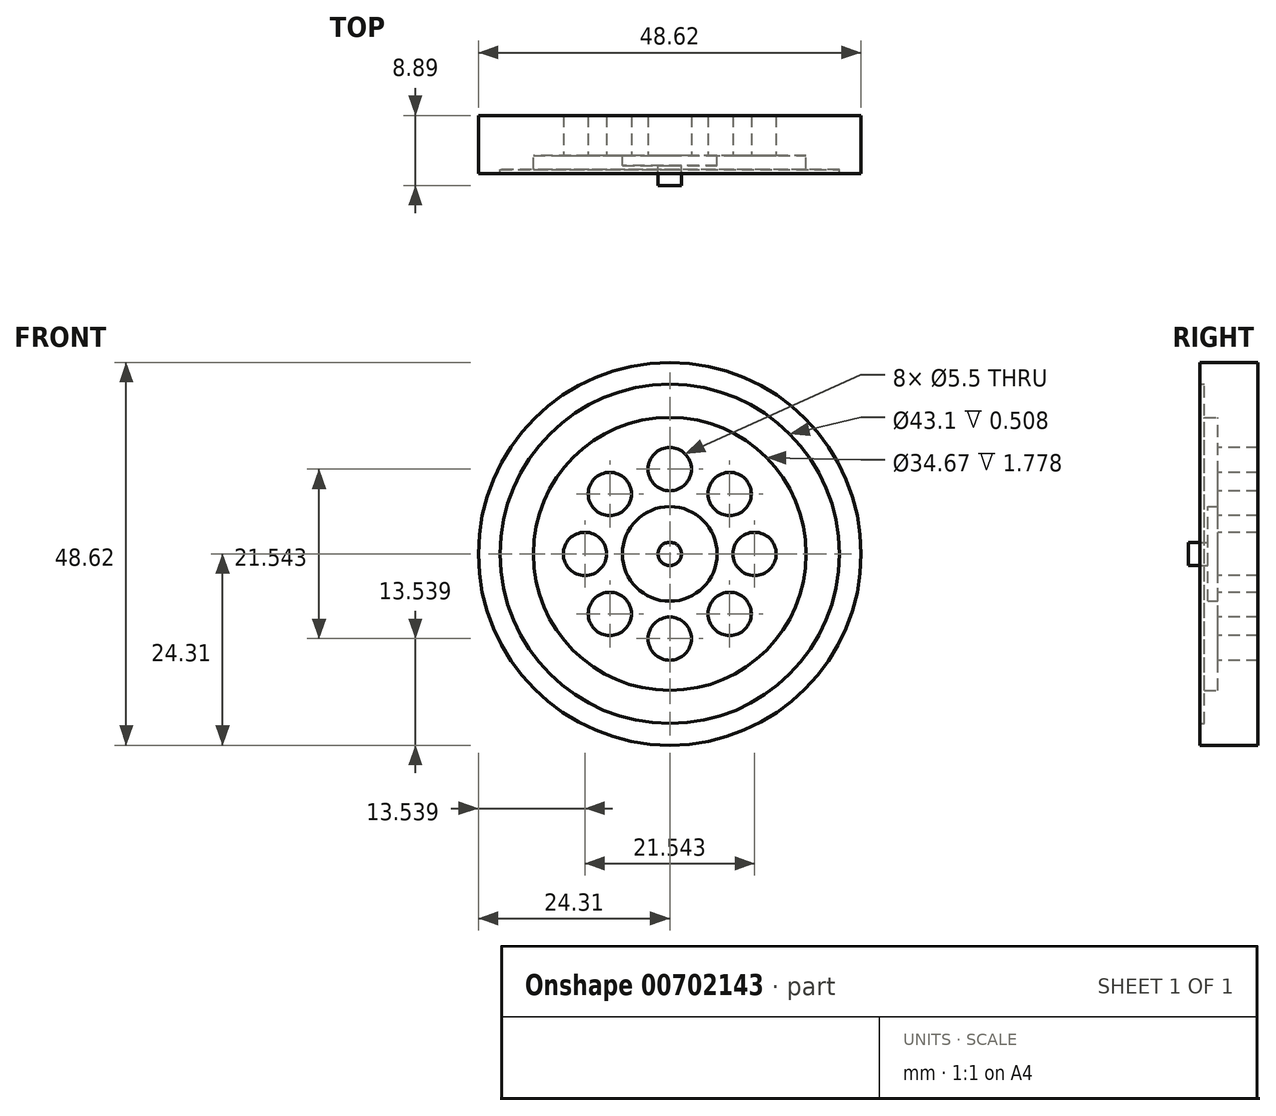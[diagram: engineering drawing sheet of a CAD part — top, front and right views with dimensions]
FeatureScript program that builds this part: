
annotation { "Feature Type Name" : "Feature", "Feature Type Description" : "" }
export const myFeature = defineFeature(function(context is Context, id is Id, definition is map)
    precondition{}
    {
        {
            var Q0;
            Q0=qCreatedBy(makeId("Front.planeOp"),FACE);
            var sketch = newSketch(context, id + "F0", { "sketchPlane" : qUnion([Q0])});
            skCircle(sketch, "E0", {"center": v(0, 0) * mm, "radius": 24.3 * mm});
            skSolve(sketch);
        }
        {
            var Q0;
            Q0=makeQuery(id+"F0.imprint","IMPRINT",FACE,{"disambiguationData":[TD([[makeQuery(id+"F0.imprint","IMPRINT",EDGE,{"derivedFrom":sQuery(id+"F0.wireOp",EDGE,"E0")}),1.0]])]});
            extrude(context, id + "F1", {"entities" : qUnion([Q0]), "depth" : 5.08 * mm, "offsetDistance" : 25.4 * mm});
        }
        {
            var Q0;
            Q0=makeQuery(id+"F1.opExtrude","CAP_FACE",FACE,{"disambiguationData":[OSD([sQuery(id+"F0.wireOp",EDGE,"E0")])],"isStart":false});
            var sketch = newSketch(context, id + "F2", { "sketchPlane" : qUnion([Q0])});
            skCircle(sketch, "E1", {"center": v(0, 0) * mm, "radius": 21.55 * mm});
            skSolve(sketch);
        }
        {
            var Q0;
            Q0=makeQuery(id+"F2.imprint","IMPRINT",FACE,{"disambiguationData":[TD([[makeQuery(id+"F2.imprint","IMPRINT",EDGE,{"derivedFrom":sQuery(id+"F2.wireOp",EDGE,"E1")}),1.0]])]});
            var sketch = newSketch(context, id + "F3", { "sketchPlane" : qUnion([Q0])});
            skCircle(sketch, "E2", {"center": v(0, 0) * mm, "radius": 6 * mm});
            skSolve(sketch);
        }
        {
            var Q0;
            Q0=makeQuery(id+"F2.imprint","IMPRINT",FACE,{"disambiguationData":[TD([[makeQuery(id+"F2.imprint","IMPRINT",EDGE,{"derivedFrom":sQuery(id+"F2.wireOp",EDGE,"E1")}),1.0]])]});
            var sketch = newSketch(context, id + "F4", { "sketchPlane" : qUnion([Q0])});
            skCircle(sketch, "E3", {"center": v(0, 0) * mm, "radius": 17.33 * mm});
            skSolve(sketch);
        }
        {
            var Q0;
            Q0=makeQuery(id+"F2.imprint","IMPRINT",FACE,{"disambiguationData":[TD([[makeQuery(id+"F2.imprint","IMPRINT",EDGE,{"derivedFrom":sQuery(id+"F2.wireOp",EDGE,"E1")}),-1.0]])]});
            extrude(context, id + "F5", {"entities" : qUnion([Q0]), "operationType" : NewBodyOperationType.ADD, "depth" : 2.3 * mm, "offsetDistance" : 25.4 * mm});
        }
        {
            var Q0;
            Q0=makeQuery(id+"F4.imprint","IMPRINT",FACE,{"disambiguationData":[TD([[makeQuery(id+"F4.imprint","IMPRINT",EDGE,{"derivedFrom":sQuery(id+"F4.wireOp",EDGE,"E3")}),-1.0]])]});
            extrude(context, id + "F6", {"entities" : qUnion([Q0]), "operationType" : NewBodyOperationType.ADD, "depth" : 1.78 * mm, "offsetDistance" : 25.4 * mm});
        }
        {
            var Q0;
            Q0=makeQuery(id+"F3.imprint","IMPRINT",FACE,{"disambiguationData":[TD([[makeQuery(id+"F3.imprint","IMPRINT",EDGE,{"derivedFrom":sQuery(id+"F3.wireOp",EDGE,"E2")}),1.0]])]});
            extrude(context, id + "F7", {"entities" : qUnion([Q0]), "operationType" : NewBodyOperationType.ADD, "depth" : 1.27 * mm, "offsetDistance" : 25.4 * mm});
        }
        {
            var Q0;
            Q0=makeQuery(id+"F7.opExtrude","CAP_FACE",FACE,{"disambiguationData":[OSD([sQuery(id+"F3.wireOp",EDGE,"E2")])],"isStart":false});
            var sketch = newSketch(context, id + "F8", { "sketchPlane" : qUnion([Q0])});
            skCircle(sketch, "E4", {"center": v(0, 0) * mm, "radius": 1.48 * mm});
            skSolve(sketch);
        }
        {
            var Q0;
            Q0=makeQuery(id+"F8.imprint","IMPRINT",FACE,{"disambiguationData":[TD([[makeQuery(id+"F8.imprint","IMPRINT",EDGE,{"derivedFrom":sQuery(id+"F8.wireOp",EDGE,"E4")}),1.0]])]});
            extrude(context, id + "F9", {"entities" : qUnion([Q0]), "operationType" : NewBodyOperationType.ADD, "depth" : 2.54 * mm, "offsetDistance" : 25.4 * mm});
        }
        {
            var Q0;
            Q0=makeQuery(id+"F1.opExtrude","CAP_FACE",FACE,{"disambiguationData":[OSD([sQuery(id+"F0.wireOp",EDGE,"E0")])],"isStart":false});
            var sketch = newSketch(context, id + "F10", { "sketchPlane" : qUnion([Q0])});
            skCircle(sketch, "E5", {"center": v(0, 10.77) * mm, "radius": 2.75 * mm});
            skCircle(sketch, "E6.1.0", {"center": v(-7.62, 7.62) * mm, "radius": 2.75 * mm});
            skCircle(sketch, "E6.2.0", {"center": v(-10.77, 0) * mm, "radius": 2.75 * mm});
            skCircle(sketch, "E6.3.0", {"center": v(-7.62, -7.62) * mm, "radius": 2.75 * mm});
            skCircle(sketch, "E6.4.0", {"center": v(0, -10.77) * mm, "radius": 2.75 * mm});
            skCircle(sketch, "E6.5.0", {"center": v(7.62, -7.62) * mm, "radius": 2.75 * mm});
            skCircle(sketch, "E6.6.0", {"center": v(10.77, 0) * mm, "radius": 2.75 * mm});
            skCircle(sketch, "E6.7.0", {"center": v(7.62, 7.62) * mm, "radius": 2.75 * mm});
            skPoint(sketch, "E6.center", {"position": v(0, 0) * mm});
            skSolve(sketch);
        }
        {
            var Q0;
            Q0=makeQuery(id+"F10.imprint","IMPRINT",FACE,{"disambiguationData":[TD([[makeQuery(id+"F10.imprint","IMPRINT",EDGE,{"derivedFrom":sQuery(id+"F10.wireOp",EDGE,"E5")}),1.0]])]});
            var Q1;
            Q1=makeQuery(id+"F10.imprint","IMPRINT",FACE,{"disambiguationData":[TD([[makeQuery(id+"F10.imprint","IMPRINT",EDGE,{"derivedFrom":sQuery(id+"F10.wireOp",EDGE,"E6.7.0")}),1.0]])]});
            var Q2;
            Q2=makeQuery(id+"F10.imprint","IMPRINT",FACE,{"disambiguationData":[TD([[makeQuery(id+"F10.imprint","IMPRINT",EDGE,{"derivedFrom":sQuery(id+"F10.wireOp",EDGE,"E6.6.0")}),1.0]])]});
            var Q3;
            Q3=makeQuery(id+"F10.imprint","IMPRINT",FACE,{"disambiguationData":[TD([[makeQuery(id+"F10.imprint","IMPRINT",EDGE,{"derivedFrom":sQuery(id+"F10.wireOp",EDGE,"E6.5.0")}),1.0]])]});
            var Q4;
            Q4=makeQuery(id+"F10.imprint","IMPRINT",FACE,{"disambiguationData":[TD([[makeQuery(id+"F10.imprint","IMPRINT",EDGE,{"derivedFrom":sQuery(id+"F10.wireOp",EDGE,"E6.4.0")}),1.0]])]});
            var Q5;
            Q5=makeQuery(id+"F10.imprint","IMPRINT",FACE,{"disambiguationData":[TD([[makeQuery(id+"F10.imprint","IMPRINT",EDGE,{"derivedFrom":sQuery(id+"F10.wireOp",EDGE,"E6.3.0")}),1.0]])]});
            var Q6;
            Q6=makeQuery(id+"F10.imprint","IMPRINT",FACE,{"disambiguationData":[TD([[makeQuery(id+"F10.imprint","IMPRINT",EDGE,{"derivedFrom":sQuery(id+"F10.wireOp",EDGE,"E6.2.0")}),1.0]])]});
            var Q7;
            Q7=makeQuery(id+"F10.imprint","IMPRINT",FACE,{"disambiguationData":[TD([[makeQuery(id+"F10.imprint","IMPRINT",EDGE,{"derivedFrom":sQuery(id+"F10.wireOp",EDGE,"E6.1.0")}),1.0]])]});
            extrude(context, id + "F11", {"entities" : qUnion([Q0, Q1, Q2, Q3, Q4, Q5, Q6, Q7]), "operationType" : NewBodyOperationType.REMOVE, "oppositeDirection" : true, "depth" : 25.4 * mm, "offsetDistance" : 25.4 * mm});
        }
    });
